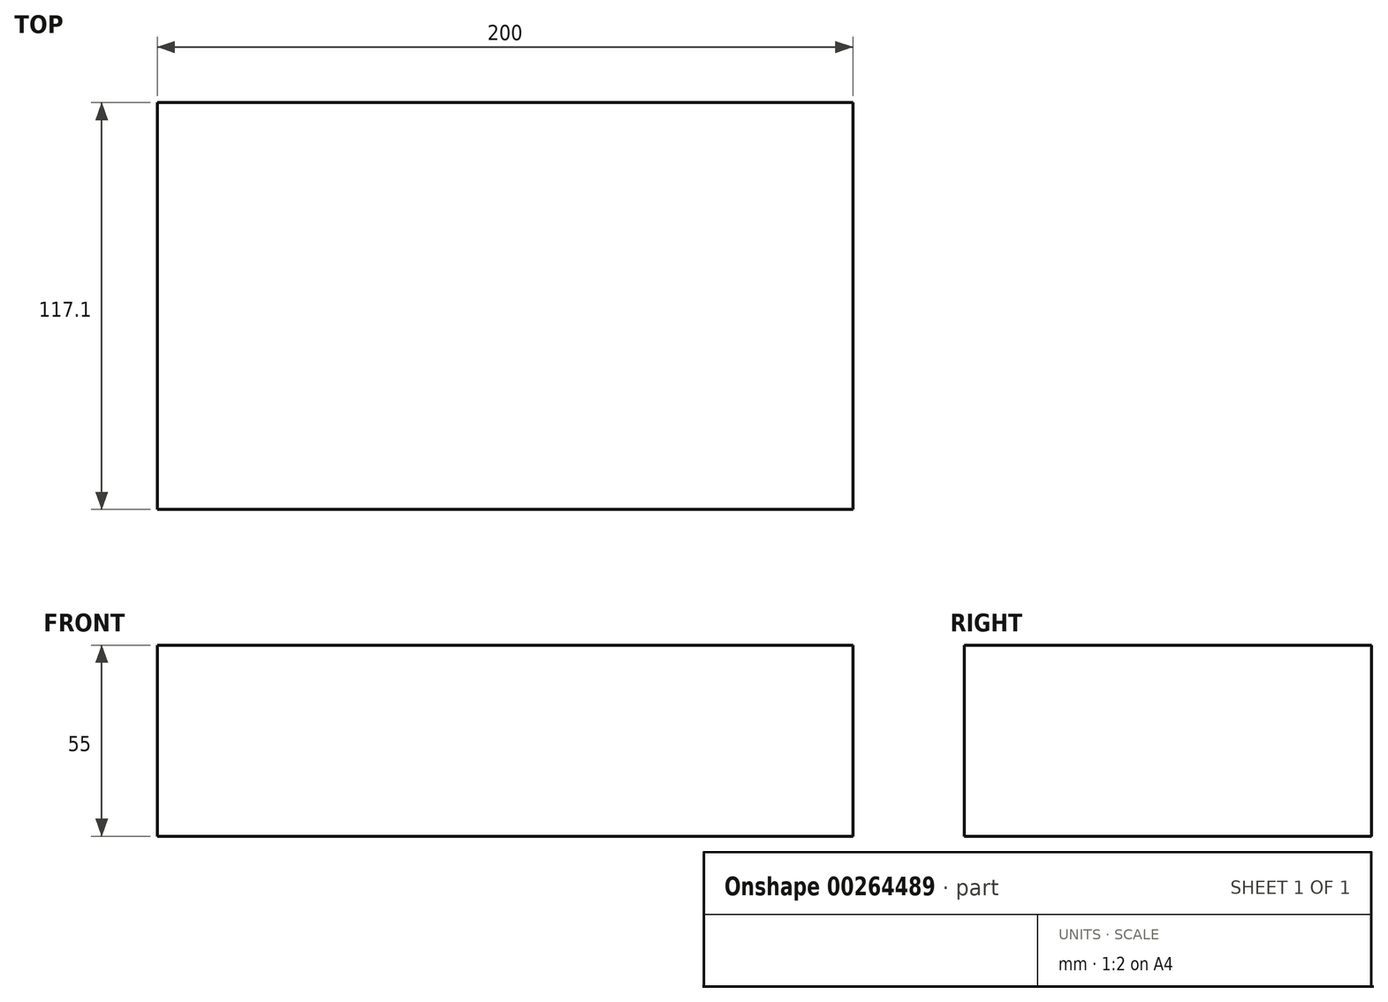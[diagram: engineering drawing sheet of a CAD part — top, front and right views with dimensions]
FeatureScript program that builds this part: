
annotation { "Feature Type Name" : "Feature", "Feature Type Description" : "" }
export const myFeature = defineFeature(function(context is Context, id is Id, definition is map)
    precondition{}
    {
        {
            var Q0;
            Q0=qCreatedBy(makeId("Top.planeOp"),FACE);
            var sketch = newSketch(context, id + "F0", { "sketchPlane" : qUnion([Q0])});
            skLineSegment(sketch, "E0.bottom", {"start": v(-100, 58.55) * mm, "end": v(100, 58.55) * mm});
            skLineSegment(sketch, "E0.top", {"start": v(-100, -58.55) * mm, "end": v(100, -58.55) * mm});
            skLineSegment(sketch, "E0.left", {"start": v(-100, 58.55) * mm, "end": v(-100, -58.55) * mm});
            skLineSegment(sketch, "E0.right", {"start": v(100, 58.55) * mm, "end": v(100, -58.55) * mm});
            skLineSegment(sketch, "E1", {"start": v(0, 58.55) * mm, "end": v(0, -58.55) * mm, "construction": true});
            skLineSegment(sketch, "E2", {"start": v(-100, 0) * mm, "end": v(100, 0) * mm, "construction": true});
            skSolve(sketch);
        }
        {
            var Q0;
            Q0=qSketchRegion(id+"F0",true);
            extrude(context, id + "F1", {"entities" : qUnion([Q0]), "depth" : 55 * mm});
        }
    });
